# Revit family: Hager-WITTY PARK-fr-FR-FR
name_source: partatom
category: Electrical Equipment
units: mm (PartAtom-declared; Revit-internal decimal feet)

## family parameters
Always vertical = Yes
Cut with Voids When Loaded = No
Host = Wall
Panel Configuration = Two Columns, Circuits Across
Part Type = Panelboard
Room Calculation Point = No
Round Connector Dimension = Use Diameter
Shared = No

## types (4) — shared parameters
BC_MODEL_ID = 1043790
BC_OBJECT_ID = 349825
BC_OBJECT_VERSION = #1
Code hager = ADD-EC002883_EVCS
Default Elevation = 1000 mm  [stored 3.28084 ft]
Ground Bus = No
HG000003-Gamme = WITTY PARK
HG000059-Operating voltage = 410 V
HG000065-Avec prise TE = No
HG000099-Onfly Template ID = 1043788
Manufacturer = hager
Name = Template-EVCS-WittyPark_EU-EC002883
Name BIM&CO = Workstation equipment
Name hager = ADD_ChargingStation_EC002883
Neutral Bus = No
avec affichage = No
avec boîte de raccordement domestique = No
avec disjoncteur de protection = No
avec gestion de la charge = No
avec interface de communication = Yes
compatible IFTTT = No
compatible avec Amazon Alexa = No
compatible avec Apple HomeKit = No
compatible avec Google Assistant = No
fonction contrôle d'accès = Yes
hauteur = 765 mm  [stored 2.50984 ft]
indice de protection (IP) = IP54
indice de protection contre les chocs (IK) = IK10
largeur = 355 mm  [stored 1.1647 ft]
matériau du boîtier/corps = autre
mode de pose = montage mural
nombre de points de chargement = 2
nombre de prises de charge type 2 = 2
nombre de prises de courant domestiques = 2
profondeur = 202 mm  [stored 0.66273 ft]
zero-valued in all types: longueur du câble de charge, nombre d'interrupteurs différentiels type A, nombre d'interrupteurs différentiels type B, nombre de coupleurs de charge CHAdeMO, nombre de coupleurs de charge GB CA, nombre de coupleurs de charge GB CC, nombre de coupleurs de charge type 1, nombre de coupleurs de charge type 1 CCS, nombre de coupleurs de charge type 2, nombre de coupleurs de charge type 2 CCS, nombre de prises CEE, nombre de prises de charge GB, nombre de prises de charge type 3

## per-type parameters (varying)
| type | BC_VARIANT_ID | HG000004-Référence fabricant | Reference description | avec compteur d'énergie | exécution raccord côté installation | puissance de raccordement nominale | puissance max. par point de chargement |
| WITTY PARK-2x7.4KW-1P-XEV600C | 842298 | XEV600C | EVSE witty park 2x7kW 1P M3T2S M2TE | Yes | monophasé | 15000 W | 7400 W |
| WITTY PARK-2x22KW-3P-XEV601 | 842300 | XEV601 | EVSE witty park 2x22kW 3P M3T2S M2TE | No | triphasé | 44000 W | 22000 W |
| WITTY PARK-2x22KW-3P-XEV601C | 842302 | XEV601C | EVSE witty park 2x22kW 3P M3T2S M2TE | Yes | triphasé | 44000 W | 22000 W |
| WITTY PARK-2x7.4KW-1P-XEV600 | 842296 | XEV600 | EVSE witty park 2x7kW 1P M3T2S M2TE | No | monophasé | 15000 W | 7400 W |

note: column(s) folded — value = type name in every type: Reference

note: [stored X ft] marks values corroborated as IEEE doubles in the binary element streams (Revit-internal decimal feet)

## geometry (parser evidence)
native form markers: Sweep x6
no freeform markers — native parametric forms only
